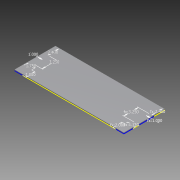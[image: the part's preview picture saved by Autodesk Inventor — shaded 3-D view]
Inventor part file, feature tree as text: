
AUTODESK INVENTOR PART (.ipt)
format: ipt  version: 2012 (Build 160160000, 160)  size: 89,088 bytes
history: native  units: in
note: dims shown in document units (in); Inventor stores cm internally (conversion verified against a paired STEP export)
features: sketch x2, extrude x1
ambient origin geometry x8: Origin, YZ Plane, XZ Plane, XY Plane, X Axis, Y Axis, Z Axis, Center Point
bodies: Solid1 (feature_tree)
feature tree (3):
  extrude  "Extrusion1"  Depth=0.2in
  sketch  "Sketch2"  dims[d2=9.0in d3=0.0in d4=1.75in d5=2.0in d6=1.75in d7=2.0in d8=2.4in d9=2.4in d10=1.0in d11=1.0in d12=3.25in d13=3.25in]
  sketch  "Sketch1"  dims[d0=24.0in d1=0.2in]
